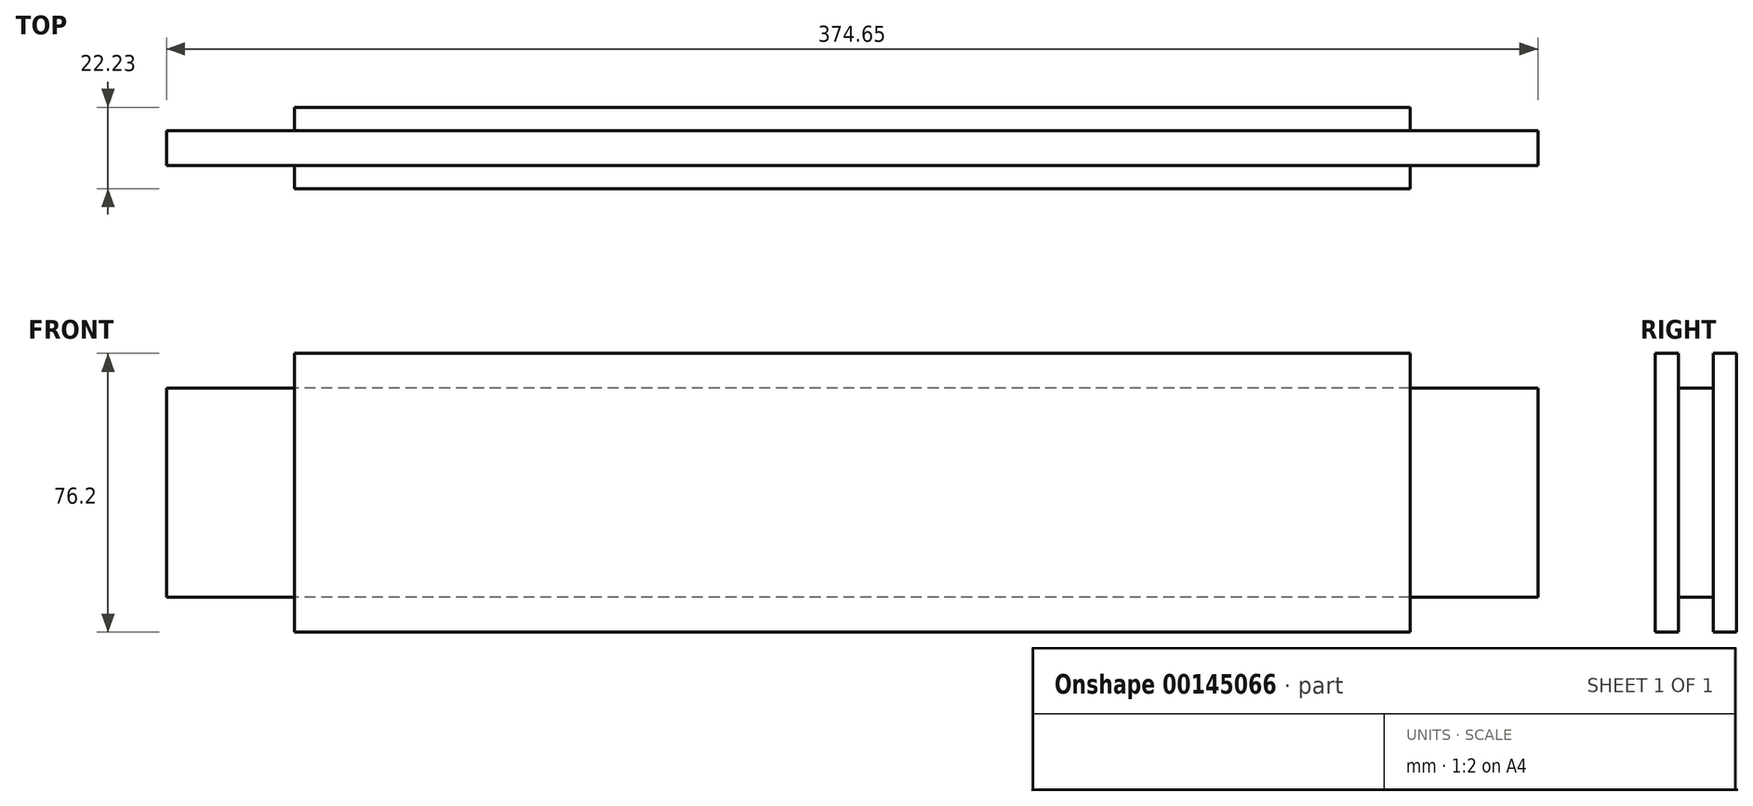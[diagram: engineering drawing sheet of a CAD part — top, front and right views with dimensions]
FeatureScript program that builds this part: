
annotation { "Feature Type Name" : "Feature", "Feature Type Description" : "" }
export const myFeature = defineFeature(function(context is Context, id is Id, definition is map)
    precondition{}
    {
        {
            var Q0;
            Q0=qCreatedBy(makeId("Front.planeOp"),FACE);
            var sketch = newSketch(context, id + "F0", { "sketchPlane" : qUnion([Q0])});
            skLineSegment(sketch, "E0.bottom", {"start": v(0, 0) * mm, "end": v(374.65, 0) * mm});
            skLineSegment(sketch, "E0.top", {"start": v(0, 76.2) * mm, "end": v(374.65, 76.2) * mm});
            skLineSegment(sketch, "E0.left", {"start": v(0, 0) * mm, "end": v(0, 76.2) * mm});
            skLineSegment(sketch, "E0.right", {"start": v(374.65, 0) * mm, "end": v(374.65, 76.2) * mm});
            skSolve(sketch);
        }
        {
            var Q0;
            Q0=makeQuery(id+"F0.imprint","IMPRINT",FACE,{"disambiguationData":[TD([[makeQuery(id+"F0.imprint","IMPRINT",EDGE,{"derivedFrom":sQuery(id+"F0.wireOp",EDGE,"E0.bottom")}),1.0]])]});
            extrude(context, id + "F1", {"entities" : qUnion([Q0]), "depth" : 22.22 * mm});
        }
        {
            var Q0;
            Q0=makeQuery(id+"F1.opExtrude","SWEPT_FACE",FACE,{"disambiguationData":[OSD([sQuery(id+"F0.wireOp",EDGE,"E0.top")])]});
            var sketch = newSketch(context, id + "F2", { "sketchPlane" : qUnion([Q0])});
            skLineSegment(sketch, "E1.bottom", {"start": v(0, 0) * mm, "end": v(34.93, 0) * mm});
            skLineSegment(sketch, "E1.top", {"start": v(0, -6.35) * mm, "end": v(34.93, -6.35) * mm});
            skLineSegment(sketch, "E1.left", {"start": v(0, 0) * mm, "end": v(0, -6.35) * mm});
            skLineSegment(sketch, "E1.right", {"start": v(34.93, 0) * mm, "end": v(34.93, -6.35) * mm});
            skLineSegment(sketch, "E2.bottom", {"start": v(0, -22.23) * mm, "end": v(34.93, -22.23) * mm});
            skLineSegment(sketch, "E2.top", {"start": v(0, -15.88) * mm, "end": v(34.93, -15.88) * mm});
            skLineSegment(sketch, "E2.left", {"start": v(0, -22.23) * mm, "end": v(0, -15.88) * mm});
            skLineSegment(sketch, "E2.right", {"start": v(34.93, -22.23) * mm, "end": v(34.93, -15.88) * mm});
            skLineSegment(sketch, "E3.bottom", {"start": v(339.73, -6.35) * mm, "end": v(374.65, -6.35) * mm});
            skLineSegment(sketch, "E3.top", {"start": v(339.73, 0) * mm, "end": v(374.65, 0) * mm});
            skLineSegment(sketch, "E3.left", {"start": v(339.73, -6.35) * mm, "end": v(339.73, 0) * mm});
            skLineSegment(sketch, "E3.right", {"start": v(374.65, -6.35) * mm, "end": v(374.65, 0) * mm});
            skLineSegment(sketch, "E4.bottom", {"start": v(339.73, -15.87) * mm, "end": v(374.65, -15.87) * mm});
            skLineSegment(sketch, "E4.top", {"start": v(339.73, -22.23) * mm, "end": v(374.65, -22.23) * mm});
            skLineSegment(sketch, "E4.left", {"start": v(339.73, -15.87) * mm, "end": v(339.73, -22.23) * mm});
            skLineSegment(sketch, "E4.right", {"start": v(374.65, -15.87) * mm, "end": v(374.65, -22.23) * mm});
            skLineSegment(sketch, "E5", {"start": v(34.93, -6.35) * mm, "end": v(339.73, -6.35) * mm});
            skLineSegment(sketch, "E6", {"start": v(34.93, -15.88) * mm, "end": v(339.73, -15.87) * mm});
            skLineSegment(sketch, "E7", {"start": v(34.93, -6.35) * mm, "end": v(34.93, -15.88) * mm});
            skLineSegment(sketch, "E8", {"start": v(339.73, -6.35) * mm, "end": v(339.73, -15.87) * mm});
            skSolve(sketch);
        }
        {
            var Q0;
            Q0=makeQuery(id+"F2.imprint","IMPRINT",FACE,{"disambiguationData":[TD([[makeQuery(id+"F2.imprint","IMPRINT",EDGE,{"derivedFrom":sQuery(id+"F2.wireOp",EDGE,"E1.bottom")}),-1.0]])]});
            var Q1;
            Q1=makeQuery(id+"F2.imprint","IMPRINT",FACE,{"disambiguationData":[TD([[makeQuery(id+"F2.imprint","IMPRINT",EDGE,{"derivedFrom":sQuery(id+"F2.wireOp",EDGE,"E2.bottom")}),1.0]])]});
            var Q2;
            Q2=makeQuery(id+"F2.imprint","IMPRINT",FACE,{"disambiguationData":[TD([[makeQuery(id+"F2.imprint","IMPRINT",EDGE,{"derivedFrom":sQuery(id+"F2.wireOp",EDGE,"E3.bottom")}),1.0]])]});
            var Q3;
            Q3=makeQuery(id+"F2.imprint","IMPRINT",FACE,{"disambiguationData":[TD([[makeQuery(id+"F2.imprint","IMPRINT",EDGE,{"derivedFrom":sQuery(id+"F2.wireOp",EDGE,"E4.bottom")}),-1.0]])]});
            extrude(context, id + "F3", {"entities" : qUnion([Q0, Q1, Q2, Q3]), "operationType" : NewBodyOperationType.REMOVE, "endBound" : BoundingType.UP_TO_NEXT, "oppositeDirection" : true, "depth" : 25.4 * mm});
        }
        {
            var Q0;
            Q0=makeQuery(id+"F1.opExtrude","SWEPT_FACE",FACE,{"disambiguationData":[OSD([sQuery(id+"F0.wireOp",EDGE,"E0.left")])]});
            var sketch = newSketch(context, id + "F4", { "sketchPlane" : qUnion([Q0])});
            skLineSegment(sketch, "E9.bottom", {"start": v(6.35, 0) * mm, "end": v(15.88, 0) * mm});
            skLineSegment(sketch, "E9.top", {"start": v(6.35, 9.53) * mm, "end": v(15.88, 9.53) * mm});
            skLineSegment(sketch, "E9.left", {"start": v(6.35, 0) * mm, "end": v(6.35, 9.53) * mm});
            skLineSegment(sketch, "E9.right", {"start": v(15.88, 0) * mm, "end": v(15.88, 9.52) * mm});
            skLineSegment(sketch, "E10.bottom", {"start": v(6.35, 76.2) * mm, "end": v(15.88, 76.2) * mm});
            skLineSegment(sketch, "E10.top", {"start": v(6.35, 66.67) * mm, "end": v(15.88, 66.67) * mm});
            skLineSegment(sketch, "E10.left", {"start": v(6.35, 76.2) * mm, "end": v(6.35, 66.67) * mm});
            skLineSegment(sketch, "E10.right", {"start": v(15.88, 76.2) * mm, "end": v(15.88, 66.67) * mm});
            skSolve(sketch);
        }
        {
            var Q0;
            Q0=makeQuery(id+"F4.imprint","IMPRINT",FACE,{"disambiguationData":[TD([[makeQuery(id+"F4.imprint","IMPRINT",EDGE,{"derivedFrom":sQuery(id+"F4.wireOp",EDGE,"E10.bottom")}),1.0]])]});
            var Q1;
            Q1=makeQuery(id+"F4.imprint","IMPRINT",FACE,{"disambiguationData":[TD([[makeQuery(id+"F4.imprint","IMPRINT",EDGE,{"derivedFrom":sQuery(id+"F4.wireOp",EDGE,"E9.bottom")}),-1.0]])]});
            extrude(context, id + "F5", {"entities" : qUnion([Q0, Q1]), "operationType" : NewBodyOperationType.REMOVE, "endBound" : BoundingType.UP_TO_NEXT, "oppositeDirection" : true, "depth" : 25.4 * mm});
        }
    });
